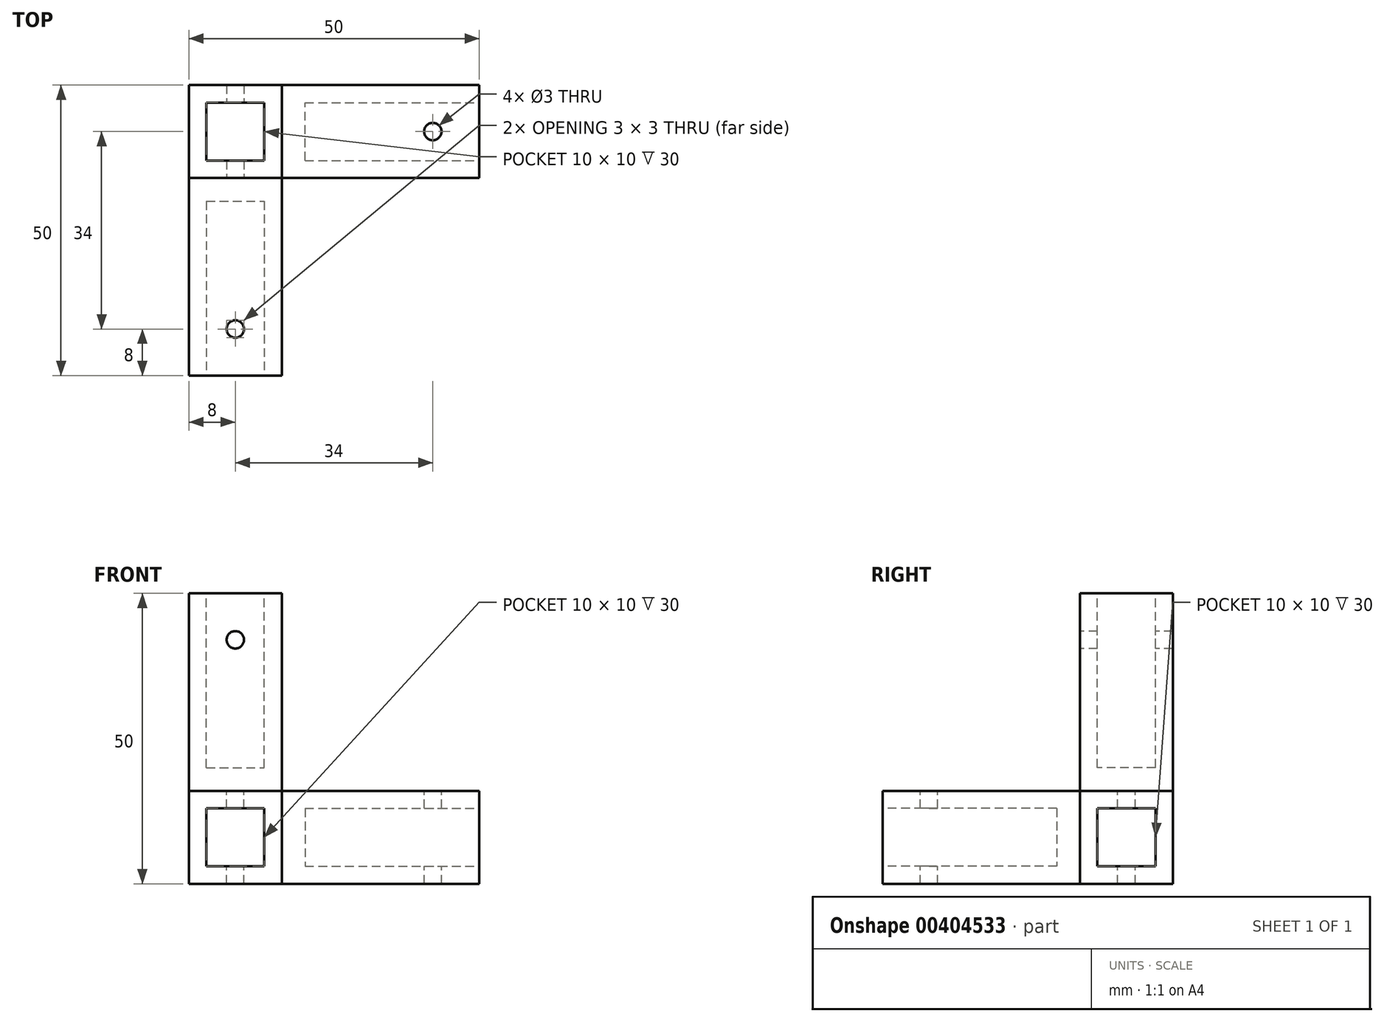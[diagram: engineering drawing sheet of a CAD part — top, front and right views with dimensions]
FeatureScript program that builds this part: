
annotation { "Feature Type Name" : "Feature", "Feature Type Description" : "" }
export const myFeature = defineFeature(function(context is Context, id is Id, definition is map)
    precondition{}
    {
        {
            var Q0;
            Q0=qCreatedBy(makeId("Top.planeOp"),FACE);
            var sketch = newSketch(context, id + "F0", { "sketchPlane" : qUnion([Q0])});
            skLineSegment(sketch, "E0.bottom", {"start": v(-25, 16) * mm, "end": v(25, 16) * mm});
            skLineSegment(sketch, "E0.top", {"start": v(-25, 0) * mm, "end": v(25, 0) * mm});
            skLineSegment(sketch, "E0.left", {"start": v(-25, 16) * mm, "end": v(-25, 0) * mm});
            skLineSegment(sketch, "E0.right", {"start": v(25, 16) * mm, "end": v(25, 0) * mm});
            skLineSegment(sketch, "E1.bottom", {"start": v(-25, 0) * mm, "end": v(-9, 0) * mm});
            skLineSegment(sketch, "E1.top", {"start": v(-25, -34) * mm, "end": v(-9, -34) * mm});
            skLineSegment(sketch, "E1.left", {"start": v(-25, 0) * mm, "end": v(-25, -34) * mm});
            skLineSegment(sketch, "E1.right", {"start": v(-9, 0) * mm, "end": v(-9, -34) * mm});
            skSolve(sketch);
        }
        {
            var Q0;
            Q0=qSketchRegion(id+"F0",true);
            extrude(context, id + "F1", {"entities" : qUnion([Q0]), "depth" : 16 * mm});
        }
        {
            var Q0;
            Q0=makeQuery(id+"F1.opExtrude","SWEPT_FACE",FACE,{"disambiguationData":[OSD([sQuery(id+"F0.wireOp",EDGE,"E0.right")])]});
            var sketch = newSketch(context, id + "F2", { "sketchPlane" : qUnion([Q0])});
            skLineSegment(sketch, "E2.bottom", {"start": v(3, 13) * mm, "end": v(13, 13) * mm});
            skLineSegment(sketch, "E2.top", {"start": v(3, 3) * mm, "end": v(13, 3) * mm});
            skLineSegment(sketch, "E2.left", {"start": v(3, 13) * mm, "end": v(3, 3) * mm});
            skLineSegment(sketch, "E2.right", {"start": v(13, 13) * mm, "end": v(13, 3) * mm});
            skSolve(sketch);
        }
        {
            var Q0;
            Q0=qSketchRegion(id+"F2",true);
            extrude(context, id + "F3", {"entities" : qUnion([Q0]), "operationType" : NewBodyOperationType.REMOVE, "oppositeDirection" : true, "depth" : 30 * mm});
        }
        {
            var Q0;
            Q0=makeQuery(id+"F1.opExtrude","SWEPT_FACE",FACE,{"disambiguationData":[OSD([sQuery(id+"F0.wireOp",EDGE,"E1.top")])]});
            var sketch = newSketch(context, id + "F4", { "sketchPlane" : qUnion([Q0])});
            skLineSegment(sketch, "E3.bottom", {"start": v(-22, 13) * mm, "end": v(-12, 13) * mm});
            skLineSegment(sketch, "E3.top", {"start": v(-22, 3) * mm, "end": v(-12, 3) * mm});
            skLineSegment(sketch, "E3.left", {"start": v(-22, 13) * mm, "end": v(-22, 3) * mm});
            skLineSegment(sketch, "E3.right", {"start": v(-12, 13) * mm, "end": v(-12, 3) * mm});
            skSolve(sketch);
        }
        {
            var Q0;
            Q0=qSketchRegion(id+"F4",true);
            extrude(context, id + "F5", {"entities" : qUnion([Q0]), "operationType" : NewBodyOperationType.REMOVE, "oppositeDirection" : true, "depth" : 30 * mm});
        }
        {
            var Q0;
            Q0=makeQuery(id+"F1.opExtrude","CAP_FACE",FACE,{"disambiguationData":[OSD([sQuery(id+"F0.wireOp",EDGE,"E0.bottom"),sQuery(id+"F0.wireOp",EDGE,"E0.top"),sQuery(id+"F0.wireOp",EDGE,"E0.left"),sQuery(id+"F0.wireOp",EDGE,"E0.right"),sQuery(id+"F0.wireOp",EDGE,"E1.top"),sQuery(id+"F0.wireOp",EDGE,"E1.left"),sQuery(id+"F0.wireOp",EDGE,"E1.right")])],"isStart":false});
            var sketch = newSketch(context, id + "F6", { "sketchPlane" : qUnion([Q0])});
            skCircle(sketch, "E4", {"center": v(-17, -26) * mm, "radius": 1.5 * mm});
            skCircle(sketch, "E5", {"center": v(17, 8) * mm, "radius": 1.5 * mm});
            skSolve(sketch);
        }
        {
            var Q0;
            Q0=qSketchRegion(id+"F6",true);
            extrude(context, id + "F7", {"entities" : qUnion([Q0]), "operationType" : NewBodyOperationType.REMOVE, "oppositeDirection" : true, "depth" : 16 * mm});
        }
        {
            var Q0;
            Q0=makeQuery(id+"F1.opExtrude","CAP_FACE",FACE,{"disambiguationData":[OSD([sQuery(id+"F0.wireOp",EDGE,"E0.bottom"),sQuery(id+"F0.wireOp",EDGE,"E0.top"),sQuery(id+"F0.wireOp",EDGE,"E0.left"),sQuery(id+"F0.wireOp",EDGE,"E0.right"),sQuery(id+"F0.wireOp",EDGE,"E1.top"),sQuery(id+"F0.wireOp",EDGE,"E1.left"),sQuery(id+"F0.wireOp",EDGE,"E1.right")])],"isStart":false});
            var sketch = newSketch(context, id + "F8", { "sketchPlane" : qUnion([Q0])});
            skLineSegment(sketch, "E6.bottom", {"start": v(-25, 16) * mm, "end": v(-9, 16) * mm});
            skLineSegment(sketch, "E6.top", {"start": v(-25, 0) * mm, "end": v(-9, 0) * mm});
            skLineSegment(sketch, "E6.left", {"start": v(-25, 16) * mm, "end": v(-25, 0) * mm});
            skLineSegment(sketch, "E6.right", {"start": v(-9, 16) * mm, "end": v(-9, 0) * mm});
            skSolve(sketch);
        }
        {
            var Q0;
            Q0 = qSketchRegion(id + "F8", true);
            extrude(context, id + "F9", {"entities" : qUnion([Q0]), "operationType" : NewBodyOperationType.ADD, "depth" : 34 * mm});
        }
        {
            var Q0;
            Q0=makeQuery(id+"F9.opExtrude","CAP_FACE",FACE,{"disambiguationData":[OSD([sQuery(id+"F8.wireOp",EDGE,"E6.bottom"),sQuery(id+"F8.wireOp",EDGE,"E6.top"),sQuery(id+"F8.wireOp",EDGE,"E6.left"),sQuery(id+"F8.wireOp",EDGE,"E6.right")])],"isStart":false});
            var sketch = newSketch(context, id + "F10", { "sketchPlane" : qUnion([Q0])});
            skLineSegment(sketch, "E7.bottom", {"start": v(-22, 13) * mm, "end": v(-12, 13) * mm});
            skLineSegment(sketch, "E7.top", {"start": v(-22, 3) * mm, "end": v(-12, 3) * mm});
            skLineSegment(sketch, "E7.left", {"start": v(-22, 13) * mm, "end": v(-22, 3) * mm});
            skLineSegment(sketch, "E7.right", {"start": v(-12, 13) * mm, "end": v(-12, 3) * mm});
            skSolve(sketch);
        }
        {
            var Q0;
            Q0 = qSketchRegion(id + "F10", true);
            extrude(context, id + "F11", {"entities" : qUnion([Q0]), "operationType" : NewBodyOperationType.REMOVE, "oppositeDirection" : true, "depth" : 30 * mm});
        }
        {
            var Q0;
            Q0=makeQuery(id+"F9.opExtrude","SWEPT_FACE",FACE,{"disambiguationData":[OSD([sQuery(id+"F8.wireOp",EDGE,"E6.top")])]});
            var sketch = newSketch(context, id + "F12", { "sketchPlane" : qUnion([Q0])});
            skCircle(sketch, "E8", {"center": v(-17, 42) * mm, "radius": 1.5 * mm});
            skSolve(sketch);
        }
        {
            var Q0;
            Q0 = qSketchRegion(id + "F12", true);
            extrude(context, id + "F13", {"entities" : qUnion([Q0]), "operationType" : NewBodyOperationType.REMOVE, "oppositeDirection" : true, "depth" : 16 * mm});
        }
    });
